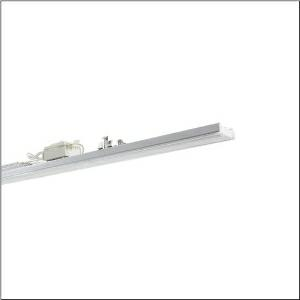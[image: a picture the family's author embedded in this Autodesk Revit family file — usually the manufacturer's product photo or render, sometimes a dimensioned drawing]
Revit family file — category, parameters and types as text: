
# Revit family: licross_r__11_recessed_mo_51te11dv4fxg_01a2
name_source: partatom
category: Lighting Fixtures
units: mm (PartAtom-declared; Revit-internal decimal feet)

## family parameters
Cut with Voids When Loaded = No
Host = Face
Light Source = No
Part Type = Normal
Room Calculation Point = No
Round Connector Dimension = Use Diameter
Shared = No

## types (1)
- --- (1 x LED, 15120 lm, 84.1 W, 4000K)
    Apparent Load = 84 VA
    CIE Flux Codes = 89 96 99 100 100
    Color Rendering = 80
    Color Temperature = 4000K
    Default Elevation = 1800 mm
    Description = Licross® 11 Recessed MO, luminaire insert, of sheet steel, galvanised, coil coated, white, length: 2.250mm, width: 66mm, height: 67mm, LED rated luminous flux: 15.120lm, light colour: 840, control gear: DALI 2, with plug, 5-pole, with phase selection, mains connection: 220..240V, AC, 50/60Hz, rated input power: 84W, halogen-free wiring, primary light control with lens, of plastic, primary optical cover: cover, of PMMA, light emission: direct distribution, primary light characteristic: symmetric, protection rating (complete): IP54, insulation class (complete): insulation class I (protective earthing), certification: CE, ENEC, VDE, UKCA, protection symbol: D if used in an environment with non-conductive dust loads with corresponding accessories, impact resistance: IK06, permissible ambient temperature for indoor applications: -25..+35°C, corresponds to IFS (International Featured Standards) requirements for safety and quality in the food industry, reducing of maximum allowable ambient temperature of 5°C with ceiling mounting, LABS conformity tested according to VDMA 24364:2018-05, packaging unit: 1 piece
    Height = 58 mm
    Lamp = 1 x LED
    Lamp Light Flux = 15120 lm
    Lamp Power = 84.1 W
    Lamp count = 1
    Length = 2250 mm
    Luminous efficacy = 180 lm/W
    Manufacturer = Siteco
    ModVariant = No
    Model = 51TE11DV4FXG
    Mounting Place = Ceiling
    Mounting Type = Pendant
    Number of Poles = 1
    OnlyDefault = Yes
    Power Factor = 1
    Product Name = Licross® 11 Recessed MO
    Product group = luminaire insert
    ProductGroupID = 902
    Protection Class = Protection class I
    Protection Degree = IP 54
    RLX_Detail_Level = 1
    RLX_Emergency_Light_Flux = 0 lm
    RLX_Emergency_Type = 0
    RLX_Emergency_Type_DB = No
    RlxData = <blob elided: 29501 chars, md5=30ddb781>
    Socket = socket
    Standby Power = 0 W
    System Light Flux = 15120 lm
    System Power = 84 W
    Type Comments = factory setting: luminous flux: 100 % | dim-lin: 254 | 378 mA
    Type Image = l_1296930.jpg
    URL = http://relux.com
    VarID = @adj_098614
    Voltage = 0 V
    Weight = 0.00 kg
    Width = 66 mm

## geometry (parser evidence)
native form markers: Blend x4, Sweep x9
no freeform markers — native parametric forms only
